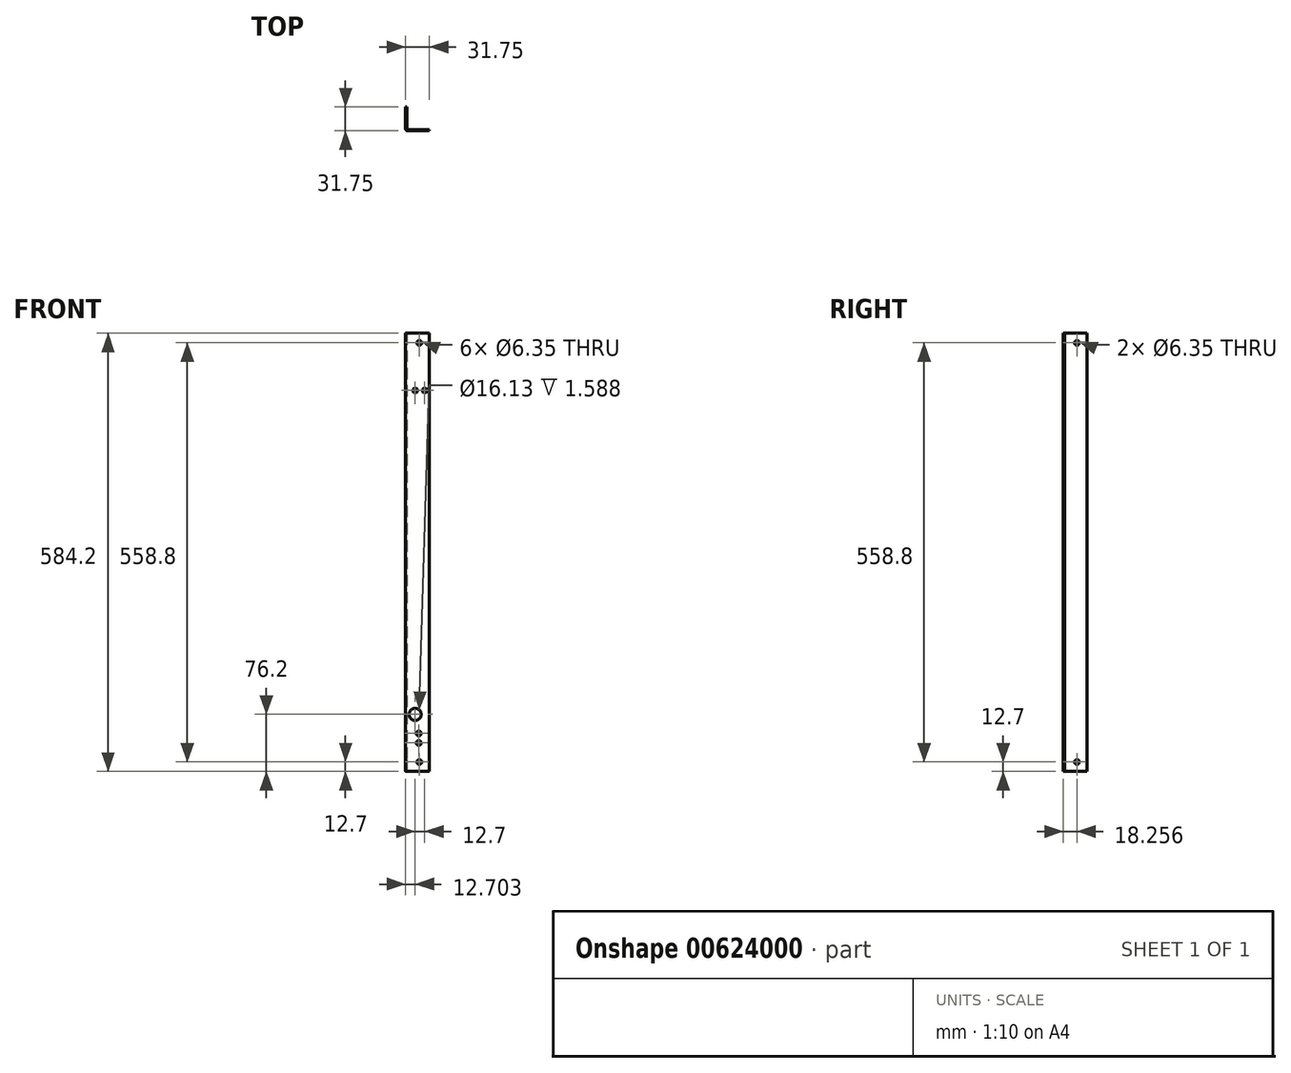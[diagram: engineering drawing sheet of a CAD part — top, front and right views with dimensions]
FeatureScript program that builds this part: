
annotation { "Feature Type Name" : "Feature", "Feature Type Description" : "" }
export const myFeature = defineFeature(function(context is Context, id is Id, definition is map)
    precondition{}
    {
        {
            var Q0;
            Q0=qCreatedBy(makeId("Top.planeOp"),FACE);
            var sketch = newSketch(context, id + "F0", { "sketchPlane" : qUnion([Q0])});
            skLineSegment(sketch, "E0", {"start": v(-5.12, 33.66) * mm, "end": v(-5.12, 3.5) * mm});
            skLineSegment(sketch, "E1", {"start": v(-5.12, 3.5) * mm, "end": v(25.04, 3.5) * mm});
            skLineSegment(sketch, "E2", {"start": v(25.04, 3.5) * mm, "end": v(25.04, 1.91) * mm});
            skLineSegment(sketch, "E3", {"start": v(25.04, 1.91) * mm, "end": v(-6.7, 1.91) * mm});
            skLineSegment(sketch, "E4", {"start": v(-6.7, 1.91) * mm, "end": v(-6.7, 33.66) * mm});
            skLineSegment(sketch, "E5", {"start": v(-6.7, 33.66) * mm, "end": v(-5.12, 33.66) * mm});
            skSolve(sketch);
        }
        {
            var Q0;
            Q0=makeQuery(id+"F0.imprint","IMPRINT",FACE,{"disambiguationData":[TD([[makeQuery(id+"F0.imprint","IMPRINT",EDGE,{"derivedFrom":sQuery(id+"F0.wireOp",EDGE,"E0")}),-1.0]])]});
            extrude(context, id + "F1", {"entities" : qUnion([Q0]), "depth" : 584.2 * mm, "offsetDistance" : 25.4 * mm});
        }
        {
            var Q0;
            Q0=makeQuery(id+"F1.opExtrude","SWEPT_EDGE",EDGE,{"disambiguationData":[OSD([sQuery(id+"F0.wireOp",EDGE,"E0"),sQuery(id+"F0.wireOp",EDGE,"E1")])]});
            var Q1;
            Q1=makeQuery(id+"F1.opExtrude","SWEPT_EDGE",EDGE,{"disambiguationData":[OSD([sQuery(id+"F0.wireOp",EDGE,"E3"),sQuery(id+"F0.wireOp",EDGE,"E4")])]});
            fillet(context, id + "F2", {"entities" : qUnion([Q0, Q1]), "radius" : 3.17 * mm, "tangentPropagation" : true, "rho" : 0.5, "crossSection" : FilletCrossSection.CONIC, "allowEdgeOverflow" : false});
        }
        {
            var Q0;
            Q0=makeQuery(id+"F1.opExtrude","SWEPT_FACE",FACE,{"disambiguationData":[OSD([sQuery(id+"F0.wireOp",EDGE,"E0")])]});
            var sketch = newSketch(context, id + "F3", { "sketchPlane" : qUnion([Q0])});
            skCircle(sketch, "E6", {"center": v(20.17, 571.5) * mm, "radius": 3.18 * mm});
            skPoint(sketch, "E6.centerSnap0", {"position": v(20.17, 584.2) * mm});
            skCircle(sketch, "E7", {"center": v(20.17, 12.7) * mm, "radius": 3.18 * mm});
            skPoint(sketch, "E7.centerSnap0", {"position": v(20.17, 0) * mm});
            skSolve(sketch);
        }
        {
            var Q0;
            Q0=makeQuery(id+"F3.imprint","IMPRINT",FACE,{"disambiguationData":[TD([[makeQuery(id+"F3.imprint","IMPRINT",EDGE,{"derivedFrom":sQuery(id+"F3.wireOp",EDGE,"E7")}),1.0]])]});
            var Q1;
            Q1=makeQuery(id+"F3.imprint","IMPRINT",FACE,{"disambiguationData":[TD([[makeQuery(id+"F3.imprint","IMPRINT",EDGE,{"derivedFrom":sQuery(id+"F3.wireOp",EDGE,"E6")}),1.0]])]});
            extrude(context, id + "F4", {"entities" : qUnion([Q0, Q1]), "operationType" : NewBodyOperationType.REMOVE, "oppositeDirection" : true, "depth" : 1.59 * mm, "offsetDistance" : 25.4 * mm});
        }
        {
            var Q0;
            Q0=makeQuery(id+"F1.opExtrude","SWEPT_FACE",FACE,{"disambiguationData":[OSD([sQuery(id+"F0.wireOp",EDGE,"E1")])]});
            var sketch = newSketch(context, id + "F5", { "sketchPlane" : qUnion([Q0])});
            skCircle(sketch, "E8", {"center": v(-11.55, 571.5) * mm, "radius": 3.18 * mm});
            skPoint(sketch, "E8.centerSnap0", {"position": v(-11.55, 584.2) * mm});
            skCircle(sketch, "E9", {"center": v(-11.55, 12.7) * mm, "radius": 3.18 * mm});
            skPoint(sketch, "E9.centerSnap0", {"position": v(-11.55, 0) * mm});
            skSolve(sketch);
        }
        {
            var Q0;
            Q0=makeQuery(id+"F5.imprint","IMPRINT",FACE,{"disambiguationData":[TD([[makeQuery(id+"F5.imprint","IMPRINT",EDGE,{"derivedFrom":sQuery(id+"F5.wireOp",EDGE,"E9")}),1.0]])]});
            var Q1;
            Q1=makeQuery(id+"F5.imprint","IMPRINT",FACE,{"disambiguationData":[TD([[makeQuery(id+"F5.imprint","IMPRINT",EDGE,{"derivedFrom":sQuery(id+"F5.wireOp",EDGE,"E8")}),1.0]])]});
            extrude(context, id + "F6", {"entities" : qUnion([Q0, Q1]), "operationType" : NewBodyOperationType.REMOVE, "oppositeDirection" : true, "depth" : 1.59 * mm, "offsetDistance" : 25.4 * mm});
        }
        {
            var Q0;
            Q0=makeQuery(id+"F1.opExtrude","SWEPT_FACE",FACE,{"disambiguationData":[OSD([sQuery(id+"F0.wireOp",EDGE,"E3")])]});
            var sketch = newSketch(context, id + "F7", { "sketchPlane" : qUnion([Q0])});
            skCircle(sketch, "E10", {"center": v(6, 508) * mm, "radius": 3.18 * mm});
            skCircle(sketch, "E11", {"center": v(18.7, 508) * mm, "radius": 3.18 * mm});
            skSolve(sketch);
        }
        {
            var Q0;
            Q0=makeQuery(id+"F7.imprint","IMPRINT",FACE,{"disambiguationData":[TD([[makeQuery(id+"F7.imprint","IMPRINT",EDGE,{"derivedFrom":sQuery(id+"F7.wireOp",EDGE,"E10")}),1.0]])]});
            var Q1;
            Q1=makeQuery(id+"F7.imprint","IMPRINT",FACE,{"disambiguationData":[TD([[makeQuery(id+"F7.imprint","IMPRINT",EDGE,{"derivedFrom":sQuery(id+"F7.wireOp",EDGE,"E11")}),1.0]])]});
            extrude(context, id + "F8", {"entities" : qUnion([Q0, Q1]), "operationType" : NewBodyOperationType.REMOVE, "oppositeDirection" : true, "depth" : 1.59 * mm, "offsetDistance" : 25.4 * mm});
        }
        {
            var Q0;
            Q0=makeQuery(id+"F1.opExtrude","SWEPT_FACE",FACE,{"disambiguationData":[OSD([sQuery(id+"F0.wireOp",EDGE,"E3")])]});
            var sketch = newSketch(context, id + "F9", { "sketchPlane" : qUnion([Q0])});
            skCircle(sketch, "E12", {"center": v(10.76, 38.1) * mm, "radius": 3.18 * mm});
            skCircle(sketch, "E13", {"center": v(10.76, 50.8) * mm, "radius": 3.18 * mm});
            skSolve(sketch);
        }
        {
            var Q0;
            Q0=makeQuery(id+"F9.imprint","IMPRINT",FACE,{"disambiguationData":[TD([[makeQuery(id+"F9.imprint","IMPRINT",EDGE,{"derivedFrom":sQuery(id+"F9.wireOp",EDGE,"E12")}),1.0]])]});
            var Q1;
            Q1=makeQuery(id+"F9.imprint","IMPRINT",FACE,{"disambiguationData":[TD([[makeQuery(id+"F9.imprint","IMPRINT",EDGE,{"derivedFrom":sQuery(id+"F9.wireOp",EDGE,"E13")}),1.0]])]});
            extrude(context, id + "F10", {"entities" : qUnion([Q0, Q1]), "operationType" : NewBodyOperationType.REMOVE, "oppositeDirection" : true, "depth" : 1.59 * mm, "offsetDistance" : 25.4 * mm});
        }
        {
            var Q0;
            Q0=makeQuery(id+"F1.opExtrude","SWEPT_FACE",FACE,{"disambiguationData":[OSD([sQuery(id+"F0.wireOp",EDGE,"E3")])]});
            var sketch = newSketch(context, id + "F11", { "sketchPlane" : qUnion([Q0])});
            skCircle(sketch, "E14", {"center": v(6, 76.2) * mm, "radius": 8.06 * mm});
            skSolve(sketch);
        }
        {
            var Q0;
            Q0=makeQuery(id+"F11.imprint","IMPRINT",FACE,{"disambiguationData":[TD([[makeQuery(id+"F11.imprint","IMPRINT",EDGE,{"derivedFrom":sQuery(id+"F11.wireOp",EDGE,"E14")}),1.0]])]});
            extrude(context, id + "F12", {"entities" : qUnion([Q0]), "operationType" : NewBodyOperationType.REMOVE, "oppositeDirection" : true, "depth" : 1.59 * mm, "offsetDistance" : 25.4 * mm});
        }
    });
